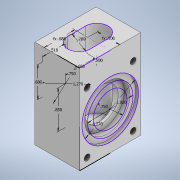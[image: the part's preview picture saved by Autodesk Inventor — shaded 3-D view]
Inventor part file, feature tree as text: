
AUTODESK INVENTOR PART (.ipt)
format: ipt  version: 2020 (Build 240168000, 168)  size: 225,280 bytes
history: native  units: in
note: dims shown in document units (in); Inventor stores cm internally (conversion verified against a paired STEP export)
features: extrude x7, sketch x4, hole x2, pattern_linear x2
ambient origin geometry x8: Origin, YZ Plane, XZ Plane, XY Plane, X Axis, Y Axis, Z Axis, Center Point
bodies: Solid1 (feature_tree)
feature tree (15):
  extrude  "Extrusion1"  Depth=0.5in
  sketch  "Sketch2"  dims[d5=0.6875in d15=0.75in]
  extrude  "Extrusion7"  Depth=0.75in
  sketch  "Sketch3"  dims[d16=1.02in d17=1.27in]
  hole  "Hole2"  [1 undecoded]
  pattern_linear  "Rectangular Pattern1"  Spacing1=0.19in  [1 undecoded]
  extrude  "Extrusion2"  Depth=0.06in TaperAngle=0.0deg
  extrude  "Extrusion3"  Depth=0.75in
  extrude  "Extrusion4"  Depth=0.19in TaperAngle=0.0deg
  sketch  "Sketch4"  dims[d18=0.0in d19=0.0in d20=0.19in d21=0.0in d22=0.06in d23=0.0in d24=0.688in d25=0.85in d26=0.75in d28=1.27in d29=0.19in d30=0.0in d31=0.06in d32=0.0in d33=0.2in d35=0.5in d36=1.75in d37=0.0in d44=0.13in d45=0.325in d46=0.375in d47=0.25in d48=0.5635in d49=0.4in d50=0.0in d51=0.7874in d53=1.035in d54=0.7874in d56=1.36in d57=0.5175in d58=0.68in d59=0.13in d60=0.325in d61=0.375in d62=0.25in d63=0.5635in d64=0.4in d65=0.0in d66=0.7874in d68=1.035in d69=0.7874in d71=1.36in d2=0.5in]
  extrude  "Extrusion5"  Depth=0.06in TaperAngle=0.0deg
  extrude  "Extrusion6"  Depth=0.5in
  hole  "Hole3"  [1 undecoded]
  pattern_linear  "Rectangular Pattern2"  Spacing1=1.75in  [1 undecoded]
  sketch  "Sketch1"  dims[d3=0.0in d4=0.5in]
note: 4 required parameter values undecoded (feature->parameter linkage not recoverable at this tier; creation-order binding heuristic only, values carry confidence <= 0.55)
